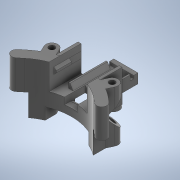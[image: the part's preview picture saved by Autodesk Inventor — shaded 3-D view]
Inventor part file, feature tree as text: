
AUTODESK INVENTOR PART (.ipt)
format: ipt  version: 2020 (Build 240168000, 168)  size: 782,848 bytes
history: native  units: mm
features: extrude x18, sketch x17, projected_geometry x15, other x5, chamfer x2, sweep x1, fillet x1
ambient origin geometry x8: Origin, YZ Plane, XZ Plane, XY Plane, X Axis, Y Axis, Z Axis, Center Point
bodies: Body1 (feature_tree)
feature tree (59):
  other  "Твердое тело1"
  extrude  "Выдавливание1"  Depth=35.0mm TaperAngle=0.0deg
  sketch  "Эскиз2"
  extrude  "Выдавливание2"  Depth=4.0mm
  sweep  "Сдвиг1"
  extrude  "Выдавливание5"  Depth=8.0mm
  extrude  "Выдавливание6"  Depth=35.0mm TaperAngle=0.0deg
  extrude  "Выдавливание7"  Depth=8.5mm
  extrude  "Выдавливание8"  TaperAngle=45.0deg  [1 undecoded]
  other  "РабПлоскость1"
  extrude  "Выдавливание9"  Depth=8.5mm
  extrude  "Выдавливание10"  TaperAngle=45.0deg  [1 undecoded]
  extrude  "Выдавливание11"  TaperAngle=0.0deg  [1 undecoded]
  sketch  "Эскиз13"
  other  "РабПлоскость2"
  sketch  "Эскиз14"
  extrude  "Выдавливание12"  Depth=5.0mm TaperAngle=0.0deg
  extrude  "Выдавливание13"  Depth=15.0mm TaperAngle=0.0deg
  other  "РабПлоскость3"
  extrude  "Выдавливание14"  Depth=15.0mm TaperAngle=0.0deg
  extrude  "Выдавливание15"  Depth=26.0mm
  extrude  "Выдавливание16"  Depth=6.0mm
  extrude  "Выдавливание17"  Depth=15.0mm TaperAngle=0.0deg
  chamfer  "Фаска1"  Distance=2.0mm
  other  "РабПлоскость4"
  sketch  "Эскиз18"
  extrude  "Выдавливание18"  Depth=1.5mm
  extrude  "Выдавливание19"  Depth=3.0mm
  extrude  "Выдавливание20"  Depth=6.0mm
  chamfer  "Фаска2"  Distance=3.5mm
  fillet  "Сопряжение1"  [1 undecoded]
  sketch  "Эскиз1"
  sketch  "Эскиз3"
  projected_geometry  "Спроецированная петля1"
  projected_geometry  "Спроецированная петля2"
  sketch  "3D эскиз1"
  sketch  "Эскиз4"
  sketch  "Эскиз6"
  projected_geometry  "Спроецированная петля4"
  sketch  "Эскиз7"
  projected_geometry  "Спроецированная петля5"
  sketch  "Эскиз9"
  projected_geometry  "Спроецированная петля7"
  sketch  "Эскиз11"
  projected_geometry  "Спроецированная петля8"
  sketch  "Эскиз12"
  projected_geometry  "Спроецированная петля9"
  projected_geometry  "Спроецированная петля10"
  sketch  "Эскиз15"
  sketch  "Эскиз16"
  projected_geometry  "Спроецированная петля11"
  projected_geometry  "Спроецированная петля12"
  sketch  "Эскиз17"
  projected_geometry  "Спроецированная петля13"
  projected_geometry  "Спроецированная петля14"
  projected_geometry  "Спроецированная петля15"
  projected_geometry  "Спроецированная петля16"
  sketch  "Эскиз19"
  projected_geometry  "Спроецированная петля17"
note: 4 required parameter values undecoded (feature->parameter linkage not recoverable at this tier; creation-order binding heuristic only, values carry confidence <= 0.55)
